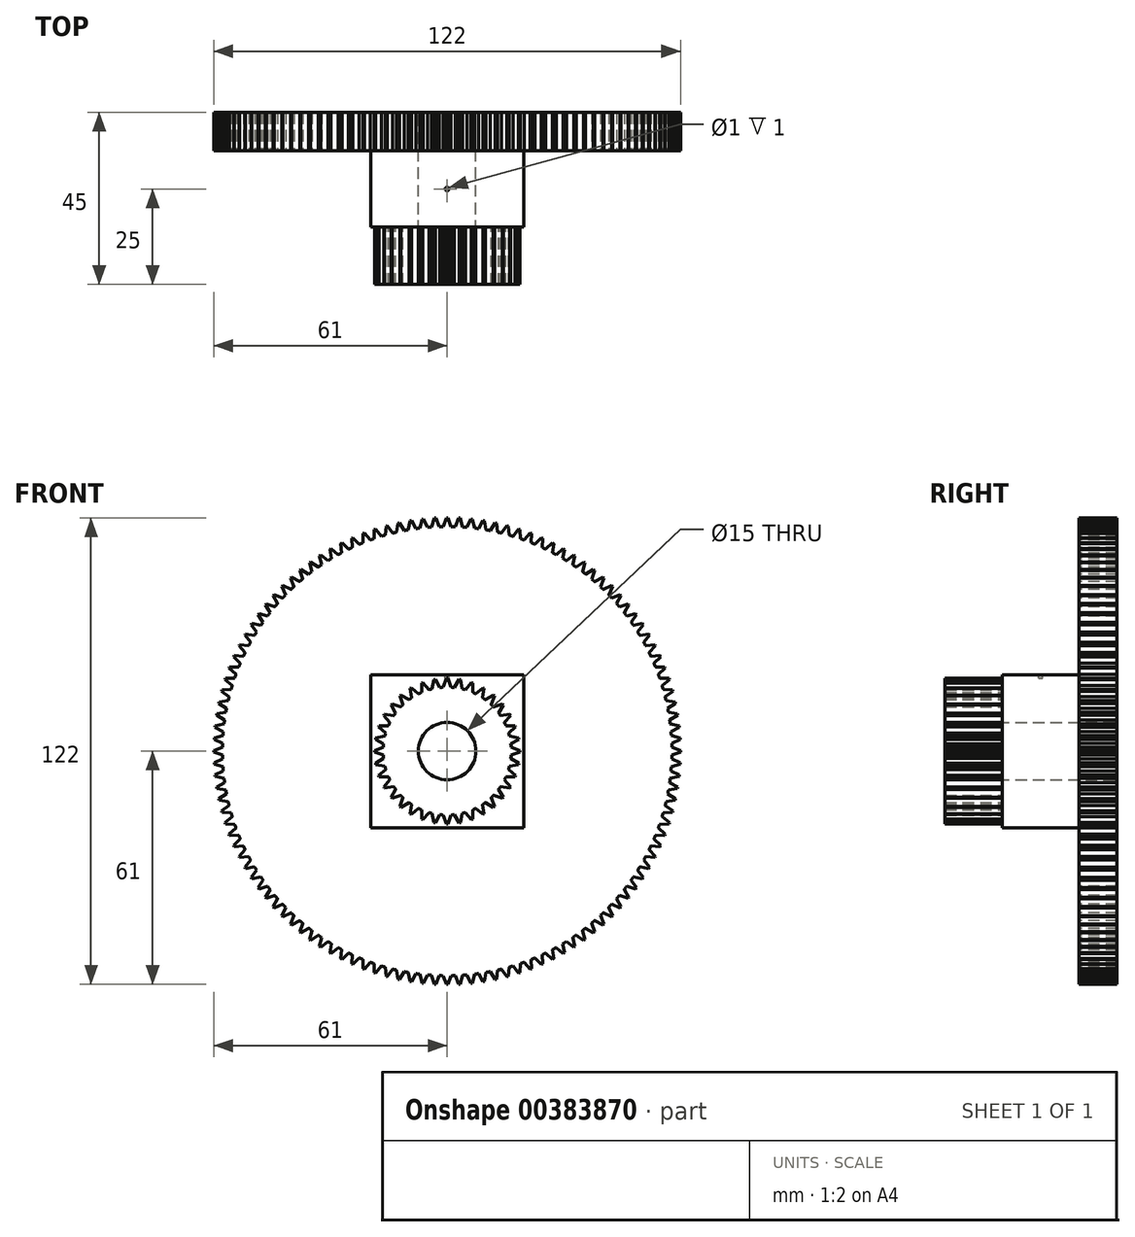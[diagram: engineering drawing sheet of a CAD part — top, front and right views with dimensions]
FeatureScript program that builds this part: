
annotation { "Feature Type Name" : "Feature", "Feature Type Description" : "" }
export const myFeature = defineFeature(function(context is Context, id is Id, definition is map)
    precondition{}
    {
        {
            var Q0;
            Q0=qCreatedBy(makeId("Front.planeOp"),FACE);
            var sketch = newSketch(context, id + "F0", { "sketchPlane" : qUnion([Q0])});
            skCircle(sketch, "E0", {"center": v(0, 0) * mm, "radius": 7.5 * mm});
            skCircle(sketch, "E1", {"center": v(0, 0) * mm, "radius": 16.75 * mm});
            skCircle(sketch, "E2", {"center": v(0, 0) * mm, "radius": 19 * mm, "construction": true});
            skLineSegment(sketch, "E3", {"start": v(-1.02, 16.72) * mm, "end": v(-0.19, 19) * mm});
            skLineSegment(sketch, "E4", {"start": v(-0.19, 19) * mm, "end": v(0, 19) * mm});
            skLineSegment(sketch, "E5", {"start": v(-1.02, 16.72) * mm, "end": v(-1.02, 19.93) * mm, "construction": true});
            skLineSegment(sketch, "E6.MirrorCS", {"start": v(0.19, 19) * mm, "end": v(0, 19) * mm});
            skLineSegment(sketch, "E7.MirrorCS", {"start": v(1.02, 16.72) * mm, "end": v(0.19, 19) * mm});
            skLineSegment(sketch, "E8.1.0", {"start": v(-3.9, 16.29) * mm, "end": v(-3.48, 18.68) * mm});
            skLineSegment(sketch, "E8.1.1", {"start": v(-3.48, 18.68) * mm, "end": v(-3.3, 18.71) * mm});
            skLineSegment(sketch, "E8.1.2", {"start": v(-3.11, 18.74) * mm, "end": v(-3.3, 18.71) * mm});
            skLineSegment(sketch, "E8.1.3", {"start": v(-1.9, 16.64) * mm, "end": v(-3.11, 18.74) * mm});
            skLineSegment(sketch, "E8.2.0", {"start": v(-6.67, 15.36) * mm, "end": v(-6.67, 17.8) * mm});
            skLineSegment(sketch, "E8.2.1", {"start": v(-6.67, 17.8) * mm, "end": v(-6.5, 17.85) * mm});
            skLineSegment(sketch, "E8.2.2", {"start": v(-6.32, 17.92) * mm, "end": v(-6.5, 17.85) * mm});
            skLineSegment(sketch, "E8.2.3", {"start": v(-4.76, 16.06) * mm, "end": v(-6.32, 17.92) * mm});
            skLineSegment(sketch, "E8.3.0", {"start": v(-9.24, 13.97) * mm, "end": v(-9.66, 16.36) * mm});
            skLineSegment(sketch, "E8.3.1", {"start": v(-9.66, 16.36) * mm, "end": v(-9.5, 16.45) * mm});
            skLineSegment(sketch, "E8.3.2", {"start": v(-9.34, 16.55) * mm, "end": v(-9.5, 16.45) * mm});
            skLineSegment(sketch, "E8.3.3", {"start": v(-7.48, 14.99) * mm, "end": v(-9.34, 16.55) * mm});
            skLineSegment(sketch, "E8.4.0", {"start": v(-11.53, 12.15) * mm, "end": v(-12.36, 14.43) * mm});
            skLineSegment(sketch, "E8.4.1", {"start": v(-12.36, 14.43) * mm, "end": v(-12.21, 14.55) * mm});
            skLineSegment(sketch, "E8.4.2", {"start": v(-12.07, 14.68) * mm, "end": v(-12.21, 14.55) * mm});
            skLineSegment(sketch, "E8.4.3", {"start": v(-9.97, 13.46) * mm, "end": v(-12.07, 14.68) * mm});
            skLineSegment(sketch, "E8.5.0", {"start": v(-13.46, 9.97) * mm, "end": v(-14.68, 12.07) * mm});
            skLineSegment(sketch, "E8.5.1", {"start": v(-14.68, 12.07) * mm, "end": v(-14.55, 12.21) * mm});
            skLineSegment(sketch, "E8.5.2", {"start": v(-14.43, 12.36) * mm, "end": v(-14.55, 12.21) * mm});
            skLineSegment(sketch, "E8.5.3", {"start": v(-12.15, 11.53) * mm, "end": v(-14.43, 12.36) * mm});
            skLineSegment(sketch, "E8.6.0", {"start": v(-14.99, 7.48) * mm, "end": v(-16.55, 9.34) * mm});
            skLineSegment(sketch, "E8.6.1", {"start": v(-16.55, 9.34) * mm, "end": v(-16.45, 9.5) * mm});
            skLineSegment(sketch, "E8.6.2", {"start": v(-16.36, 9.66) * mm, "end": v(-16.45, 9.5) * mm});
            skLineSegment(sketch, "E8.6.3", {"start": v(-13.97, 9.24) * mm, "end": v(-16.36, 9.66) * mm});
            skLineSegment(sketch, "E8.7.0", {"start": v(-16.06, 4.76) * mm, "end": v(-17.92, 6.32) * mm});
            skLineSegment(sketch, "E8.7.1", {"start": v(-17.92, 6.32) * mm, "end": v(-17.85, 6.5) * mm});
            skLineSegment(sketch, "E8.7.2", {"start": v(-17.8, 6.67) * mm, "end": v(-17.85, 6.5) * mm});
            skLineSegment(sketch, "E8.7.3", {"start": v(-15.36, 6.67) * mm, "end": v(-17.8, 6.67) * mm});
            skLineSegment(sketch, "E8.8.0", {"start": v(-16.64, 1.9) * mm, "end": v(-18.74, 3.11) * mm});
            skLineSegment(sketch, "E8.8.1", {"start": v(-18.74, 3.11) * mm, "end": v(-18.71, 3.3) * mm});
            skLineSegment(sketch, "E8.8.2", {"start": v(-18.68, 3.48) * mm, "end": v(-18.71, 3.3) * mm});
            skLineSegment(sketch, "E8.8.3", {"start": v(-16.29, 3.9) * mm, "end": v(-18.68, 3.48) * mm});
            skLineSegment(sketch, "E8.9.0", {"start": v(-16.72, -1.02) * mm, "end": v(-19, -0.19) * mm});
            skLineSegment(sketch, "E8.9.1", {"start": v(-19, -0.19) * mm, "end": v(-19, 0) * mm});
            skLineSegment(sketch, "E8.9.2", {"start": v(-19, 0.19) * mm, "end": v(-19, 0) * mm});
            skLineSegment(sketch, "E8.9.3", {"start": v(-16.72, 1.02) * mm, "end": v(-19, 0.19) * mm});
            skLineSegment(sketch, "E8.10.0", {"start": v(-16.29, -3.9) * mm, "end": v(-18.68, -3.48) * mm});
            skLineSegment(sketch, "E8.10.1", {"start": v(-18.68, -3.48) * mm, "end": v(-18.71, -3.3) * mm});
            skLineSegment(sketch, "E8.10.2", {"start": v(-18.74, -3.11) * mm, "end": v(-18.71, -3.3) * mm});
            skLineSegment(sketch, "E8.10.3", {"start": v(-16.64, -1.9) * mm, "end": v(-18.74, -3.11) * mm});
            skLineSegment(sketch, "E8.11.0", {"start": v(-15.36, -6.67) * mm, "end": v(-17.8, -6.67) * mm});
            skLineSegment(sketch, "E8.11.1", {"start": v(-17.8, -6.67) * mm, "end": v(-17.85, -6.5) * mm});
            skLineSegment(sketch, "E8.11.2", {"start": v(-17.92, -6.32) * mm, "end": v(-17.85, -6.5) * mm});
            skLineSegment(sketch, "E8.11.3", {"start": v(-16.06, -4.76) * mm, "end": v(-17.92, -6.32) * mm});
            skLineSegment(sketch, "E9.1.12.0", {"start": v(-13.97, -9.24) * mm, "end": v(-16.36, -9.66) * mm});
            skLineSegment(sketch, "E9.3.12.0", {"start": v(-16.36, -9.66) * mm, "end": v(-16.45, -9.5) * mm});
            skLineSegment(sketch, "E9.6.12.0", {"start": v(-16.55, -9.34) * mm, "end": v(-16.45, -9.5) * mm});
            skLineSegment(sketch, "E9.9.12.0", {"start": v(-14.99, -7.48) * mm, "end": v(-16.55, -9.34) * mm});
            skLineSegment(sketch, "E9.1.13.0", {"start": v(-12.15, -11.53) * mm, "end": v(-14.43, -12.36) * mm});
            skLineSegment(sketch, "E9.3.13.0", {"start": v(-14.43, -12.36) * mm, "end": v(-14.55, -12.21) * mm});
            skLineSegment(sketch, "E9.6.13.0", {"start": v(-14.68, -12.07) * mm, "end": v(-14.55, -12.21) * mm});
            skLineSegment(sketch, "E9.9.13.0", {"start": v(-13.46, -9.97) * mm, "end": v(-14.68, -12.07) * mm});
            skLineSegment(sketch, "E9.1.14.0", {"start": v(-9.97, -13.46) * mm, "end": v(-12.07, -14.68) * mm});
            skLineSegment(sketch, "E9.3.14.0", {"start": v(-12.07, -14.68) * mm, "end": v(-12.21, -14.55) * mm});
            skLineSegment(sketch, "E9.6.14.0", {"start": v(-12.36, -14.43) * mm, "end": v(-12.21, -14.55) * mm});
            skLineSegment(sketch, "E9.9.14.0", {"start": v(-11.53, -12.15) * mm, "end": v(-12.36, -14.43) * mm});
            skLineSegment(sketch, "E9.1.15.0", {"start": v(-7.48, -14.99) * mm, "end": v(-9.34, -16.55) * mm});
            skLineSegment(sketch, "E9.3.15.0", {"start": v(-9.34, -16.55) * mm, "end": v(-9.5, -16.45) * mm});
            skLineSegment(sketch, "E9.6.15.0", {"start": v(-9.66, -16.36) * mm, "end": v(-9.5, -16.45) * mm});
            skLineSegment(sketch, "E9.9.15.0", {"start": v(-9.24, -13.97) * mm, "end": v(-9.66, -16.36) * mm});
            skLineSegment(sketch, "E9.1.16.0", {"start": v(-4.76, -16.06) * mm, "end": v(-6.32, -17.92) * mm});
            skLineSegment(sketch, "E9.3.16.0", {"start": v(-6.32, -17.92) * mm, "end": v(-6.5, -17.85) * mm});
            skLineSegment(sketch, "E9.6.16.0", {"start": v(-6.67, -17.8) * mm, "end": v(-6.5, -17.85) * mm});
            skLineSegment(sketch, "E9.9.16.0", {"start": v(-6.67, -15.36) * mm, "end": v(-6.67, -17.8) * mm});
            skLineSegment(sketch, "E9.1.17.0", {"start": v(-1.9, -16.64) * mm, "end": v(-3.11, -18.74) * mm});
            skLineSegment(sketch, "E9.3.17.0", {"start": v(-3.11, -18.74) * mm, "end": v(-3.3, -18.71) * mm});
            skLineSegment(sketch, "E9.6.17.0", {"start": v(-3.48, -18.68) * mm, "end": v(-3.3, -18.71) * mm});
            skLineSegment(sketch, "E9.9.17.0", {"start": v(-3.9, -16.29) * mm, "end": v(-3.48, -18.68) * mm});
            skLineSegment(sketch, "E9.1.18.0", {"start": v(1.02, -16.72) * mm, "end": v(0.19, -19) * mm});
            skLineSegment(sketch, "E9.3.18.0", {"start": v(0.19, -19) * mm, "end": v(0, -19) * mm});
            skLineSegment(sketch, "E9.6.18.0", {"start": v(-0.19, -19) * mm, "end": v(0, -19) * mm});
            skLineSegment(sketch, "E9.9.18.0", {"start": v(-1.02, -16.72) * mm, "end": v(-0.19, -19) * mm});
            skLineSegment(sketch, "E9.1.19.0", {"start": v(3.9, -16.29) * mm, "end": v(3.48, -18.68) * mm});
            skLineSegment(sketch, "E9.3.19.0", {"start": v(3.48, -18.68) * mm, "end": v(3.3, -18.71) * mm});
            skLineSegment(sketch, "E9.6.19.0", {"start": v(3.11, -18.74) * mm, "end": v(3.3, -18.71) * mm});
            skLineSegment(sketch, "E9.9.19.0", {"start": v(1.9, -16.64) * mm, "end": v(3.11, -18.74) * mm});
            skLineSegment(sketch, "E9.1.20.0", {"start": v(6.67, -15.36) * mm, "end": v(6.67, -17.8) * mm});
            skLineSegment(sketch, "E9.3.20.0", {"start": v(6.67, -17.8) * mm, "end": v(6.5, -17.85) * mm});
            skLineSegment(sketch, "E9.6.20.0", {"start": v(6.32, -17.92) * mm, "end": v(6.5, -17.85) * mm});
            skLineSegment(sketch, "E9.9.20.0", {"start": v(4.76, -16.06) * mm, "end": v(6.32, -17.92) * mm});
            skLineSegment(sketch, "E9.1.21.0", {"start": v(9.24, -13.97) * mm, "end": v(9.66, -16.36) * mm});
            skLineSegment(sketch, "E9.3.21.0", {"start": v(9.66, -16.36) * mm, "end": v(9.5, -16.45) * mm});
            skLineSegment(sketch, "E9.6.21.0", {"start": v(9.34, -16.55) * mm, "end": v(9.5, -16.45) * mm});
            skLineSegment(sketch, "E9.9.21.0", {"start": v(7.48, -14.99) * mm, "end": v(9.34, -16.55) * mm});
            skLineSegment(sketch, "E9.1.22.0", {"start": v(11.53, -12.15) * mm, "end": v(12.36, -14.43) * mm});
            skLineSegment(sketch, "E9.3.22.0", {"start": v(12.36, -14.43) * mm, "end": v(12.21, -14.55) * mm});
            skLineSegment(sketch, "E9.6.22.0", {"start": v(12.07, -14.68) * mm, "end": v(12.21, -14.55) * mm});
            skLineSegment(sketch, "E9.9.22.0", {"start": v(9.97, -13.46) * mm, "end": v(12.07, -14.68) * mm});
            skLineSegment(sketch, "E9.1.23.0", {"start": v(13.46, -9.97) * mm, "end": v(14.68, -12.07) * mm});
            skLineSegment(sketch, "E9.3.23.0", {"start": v(14.68, -12.07) * mm, "end": v(14.55, -12.21) * mm});
            skLineSegment(sketch, "E9.6.23.0", {"start": v(14.43, -12.36) * mm, "end": v(14.55, -12.21) * mm});
            skLineSegment(sketch, "E9.9.23.0", {"start": v(12.15, -11.53) * mm, "end": v(14.43, -12.36) * mm});
            skLineSegment(sketch, "E10.1.24.0", {"start": v(14.99, -7.48) * mm, "end": v(16.55, -9.34) * mm});
            skLineSegment(sketch, "E10.3.24.0", {"start": v(16.55, -9.34) * mm, "end": v(16.45, -9.5) * mm});
            skLineSegment(sketch, "E10.6.24.0", {"start": v(16.36, -9.66) * mm, "end": v(16.45, -9.5) * mm});
            skLineSegment(sketch, "E10.9.24.0", {"start": v(13.97, -9.24) * mm, "end": v(16.36, -9.66) * mm});
            skLineSegment(sketch, "E10.1.25.0", {"start": v(16.06, -4.76) * mm, "end": v(17.92, -6.32) * mm});
            skLineSegment(sketch, "E10.3.25.0", {"start": v(17.92, -6.32) * mm, "end": v(17.85, -6.5) * mm});
            skLineSegment(sketch, "E10.6.25.0", {"start": v(17.8, -6.67) * mm, "end": v(17.85, -6.5) * mm});
            skLineSegment(sketch, "E10.9.25.0", {"start": v(15.36, -6.67) * mm, "end": v(17.8, -6.67) * mm});
            skLineSegment(sketch, "E10.1.26.0", {"start": v(16.64, -1.9) * mm, "end": v(18.74, -3.11) * mm});
            skLineSegment(sketch, "E10.3.26.0", {"start": v(18.74, -3.11) * mm, "end": v(18.71, -3.3) * mm});
            skLineSegment(sketch, "E10.6.26.0", {"start": v(18.68, -3.48) * mm, "end": v(18.71, -3.3) * mm});
            skLineSegment(sketch, "E10.9.26.0", {"start": v(16.29, -3.9) * mm, "end": v(18.68, -3.48) * mm});
            skLineSegment(sketch, "E10.1.27.0", {"start": v(16.72, 1.02) * mm, "end": v(19, 0.19) * mm});
            skLineSegment(sketch, "E10.3.27.0", {"start": v(19, 0.19) * mm, "end": v(19, 0) * mm});
            skLineSegment(sketch, "E10.6.27.0", {"start": v(19, -0.19) * mm, "end": v(19, 0) * mm});
            skLineSegment(sketch, "E10.9.27.0", {"start": v(16.72, -1.02) * mm, "end": v(19, -0.19) * mm});
            skLineSegment(sketch, "E10.1.28.0", {"start": v(16.29, 3.9) * mm, "end": v(18.68, 3.48) * mm});
            skLineSegment(sketch, "E10.3.28.0", {"start": v(18.68, 3.48) * mm, "end": v(18.71, 3.3) * mm});
            skLineSegment(sketch, "E10.6.28.0", {"start": v(18.74, 3.11) * mm, "end": v(18.71, 3.3) * mm});
            skLineSegment(sketch, "E10.9.28.0", {"start": v(16.64, 1.9) * mm, "end": v(18.74, 3.11) * mm});
            skLineSegment(sketch, "E10.1.29.0", {"start": v(15.36, 6.67) * mm, "end": v(17.8, 6.67) * mm});
            skLineSegment(sketch, "E10.3.29.0", {"start": v(17.8, 6.67) * mm, "end": v(17.85, 6.5) * mm});
            skLineSegment(sketch, "E10.6.29.0", {"start": v(17.92, 6.32) * mm, "end": v(17.85, 6.5) * mm});
            skLineSegment(sketch, "E10.9.29.0", {"start": v(16.06, 4.76) * mm, "end": v(17.92, 6.32) * mm});
            skLineSegment(sketch, "E10.1.30.0", {"start": v(13.97, 9.24) * mm, "end": v(16.36, 9.66) * mm});
            skLineSegment(sketch, "E10.3.30.0", {"start": v(16.36, 9.66) * mm, "end": v(16.45, 9.5) * mm});
            skLineSegment(sketch, "E10.6.30.0", {"start": v(16.55, 9.34) * mm, "end": v(16.45, 9.5) * mm});
            skLineSegment(sketch, "E10.9.30.0", {"start": v(14.99, 7.48) * mm, "end": v(16.55, 9.34) * mm});
            skLineSegment(sketch, "E10.1.31.0", {"start": v(12.15, 11.53) * mm, "end": v(14.43, 12.36) * mm});
            skLineSegment(sketch, "E10.3.31.0", {"start": v(14.43, 12.36) * mm, "end": v(14.55, 12.21) * mm});
            skLineSegment(sketch, "E10.6.31.0", {"start": v(14.68, 12.07) * mm, "end": v(14.55, 12.21) * mm});
            skLineSegment(sketch, "E10.9.31.0", {"start": v(13.46, 9.97) * mm, "end": v(14.68, 12.07) * mm});
            skLineSegment(sketch, "E10.1.32.0", {"start": v(9.97, 13.46) * mm, "end": v(12.07, 14.68) * mm});
            skLineSegment(sketch, "E10.3.32.0", {"start": v(12.07, 14.68) * mm, "end": v(12.21, 14.55) * mm});
            skLineSegment(sketch, "E10.6.32.0", {"start": v(12.36, 14.43) * mm, "end": v(12.21, 14.55) * mm});
            skLineSegment(sketch, "E10.9.32.0", {"start": v(11.53, 12.15) * mm, "end": v(12.36, 14.43) * mm});
            skLineSegment(sketch, "E10.1.33.0", {"start": v(7.48, 14.99) * mm, "end": v(9.34, 16.55) * mm});
            skLineSegment(sketch, "E10.3.33.0", {"start": v(9.34, 16.55) * mm, "end": v(9.5, 16.45) * mm});
            skLineSegment(sketch, "E10.6.33.0", {"start": v(9.66, 16.36) * mm, "end": v(9.5, 16.45) * mm});
            skLineSegment(sketch, "E10.9.33.0", {"start": v(9.24, 13.97) * mm, "end": v(9.66, 16.36) * mm});
            skLineSegment(sketch, "E10.1.34.0", {"start": v(4.76, 16.06) * mm, "end": v(6.32, 17.92) * mm});
            skLineSegment(sketch, "E10.3.34.0", {"start": v(6.32, 17.92) * mm, "end": v(6.5, 17.85) * mm});
            skLineSegment(sketch, "E10.6.34.0", {"start": v(6.67, 17.8) * mm, "end": v(6.5, 17.85) * mm});
            skLineSegment(sketch, "E10.9.34.0", {"start": v(6.67, 15.36) * mm, "end": v(6.67, 17.8) * mm});
            skLineSegment(sketch, "E10.1.35.0", {"start": v(1.9, 16.64) * mm, "end": v(3.11, 18.74) * mm});
            skLineSegment(sketch, "E10.3.35.0", {"start": v(3.11, 18.74) * mm, "end": v(3.3, 18.71) * mm});
            skLineSegment(sketch, "E10.6.35.0", {"start": v(3.48, 18.68) * mm, "end": v(3.3, 18.71) * mm});
            skLineSegment(sketch, "E10.9.35.0", {"start": v(3.9, 16.29) * mm, "end": v(3.48, 18.68) * mm});
            skSolve(sketch);
        }
        {
            var Q0;
            Q0=qSketchRegion(id+"F0",true);
            extrude(context, id + "F1", {"entities" : qUnion([Q0]), "depth" : 15 * mm});
        }
        {
            var Q0;
            Q0=qCreatedBy(makeId("Front.planeOp"),FACE);
            var sketch = newSketch(context, id + "F2", { "sketchPlane" : qUnion([Q0])});
            skCircle(sketch, "E11", {"center": v(0, 0) * mm, "radius": 7.5 * mm});
            skLineSegment(sketch, "E12.bottom", {"start": v(-20, -20) * mm, "end": v(20, -20) * mm});
            skLineSegment(sketch, "E12.top", {"start": v(-20, 20) * mm, "end": v(20, 20) * mm});
            skLineSegment(sketch, "E12.left", {"start": v(-20, -20) * mm, "end": v(-20, 20) * mm});
            skLineSegment(sketch, "E12.right", {"start": v(20, -20) * mm, "end": v(20, 20) * mm});
            skSolve(sketch);
        }
        {
            var Q0;
            Q0=qSketchRegion(id+"F2",true);
            extrude(context, id + "F3", {"entities" : qUnion([Q0]), "operationType" : NewBodyOperationType.ADD, "depth" : -20 * mm});
        }
        {
            var Q0;
            Q0=makeQuery(id+"F3.opExtrude","CAP_FACE",FACE,{"disambiguationData":[OSD([sQuery(id+"F2.wireOp",EDGE,"Zh5lLQ9h-1iR5-KiPg-C2Wr-JR3NM9Zv75rL"),sQuery(id+"F2.wireOp",EDGE,"E11")])],"isStart":false});
            var sketch = newSketch(context, id + "F4", { "sketchPlane" : qUnion([Q0])});
            skCircle(sketch, "E13", {"center": v(0, 0) * mm, "radius": 58.75 * mm});
            skCircle(sketch, "E14", {"center": v(0, 0) * mm, "radius": 61 * mm, "construction": true});
            skLineSegment(sketch, "E15", {"start": v(-1, 58.74) * mm, "end": v(-1, 64.16) * mm, "construction": true});
            skLineSegment(sketch, "E16", {"start": v(-1, 58.74) * mm, "end": v(-0.19, 61) * mm});
            skLineSegment(sketch, "E17", {"start": v(-0.19, 61) * mm, "end": v(0, 61) * mm});
            skLineSegment(sketch, "E18.MirrorCS", {"start": v(0.19, 61) * mm, "end": v(0, 61) * mm});
            skLineSegment(sketch, "E19.MirrorCS", {"start": v(1, 58.74) * mm, "end": v(0.19, 61) * mm});
            skLineSegment(sketch, "E20.1.0", {"start": v(-4.08, 58.6) * mm, "end": v(-3.38, 60.9) * mm});
            skLineSegment(sketch, "E20.1.1", {"start": v(-3.38, 60.9) * mm, "end": v(-3.2, 60.92) * mm});
            skLineSegment(sketch, "E20.1.2", {"start": v(-3, 60.93) * mm, "end": v(-3.2, 60.92) * mm});
            skLineSegment(sketch, "E20.1.3", {"start": v(-2.07, 58.71) * mm, "end": v(-3, 60.93) * mm});
            skLineSegment(sketch, "E20.2.0", {"start": v(-7.14, 58.31) * mm, "end": v(-6.56, 60.65) * mm});
            skLineSegment(sketch, "E20.2.1", {"start": v(-6.56, 60.65) * mm, "end": v(-6.38, 60.67) * mm});
            skLineSegment(sketch, "E20.2.2", {"start": v(-6.19, 60.69) * mm, "end": v(-6.38, 60.67) * mm});
            skLineSegment(sketch, "E20.2.3", {"start": v(-5.14, 58.53) * mm, "end": v(-6.19, 60.69) * mm});
            skLineSegment(sketch, "E20.3.0", {"start": v(-10.19, 57.86) * mm, "end": v(-9.73, 60.22) * mm});
            skLineSegment(sketch, "E20.3.1", {"start": v(-9.73, 60.22) * mm, "end": v(-9.54, 60.25) * mm});
            skLineSegment(sketch, "E20.3.2", {"start": v(-9.36, 60.28) * mm, "end": v(-9.54, 60.25) * mm});
            skLineSegment(sketch, "E20.3.3", {"start": v(-8.2, 58.18) * mm, "end": v(-9.36, 60.28) * mm});
            skLineSegment(sketch, "E20.4.0", {"start": v(-13.2, 57.25) * mm, "end": v(-12.87, 59.63) * mm});
            skLineSegment(sketch, "E20.4.1", {"start": v(-12.87, 59.63) * mm, "end": v(-12.68, 59.67) * mm});
            skLineSegment(sketch, "E20.4.2", {"start": v(-12.5, 59.7) * mm, "end": v(-12.68, 59.67) * mm});
            skLineSegment(sketch, "E20.4.3", {"start": v(-11.23, 57.67) * mm, "end": v(-12.5, 59.7) * mm});
            skLineSegment(sketch, "E20.5.0", {"start": v(-16.18, 56.48) * mm, "end": v(-15.97, 58.87) * mm});
            skLineSegment(sketch, "E20.5.1", {"start": v(-15.97, 58.87) * mm, "end": v(-15.79, 58.92) * mm});
            skLineSegment(sketch, "E20.5.2", {"start": v(-15.6, 58.97) * mm, "end": v(-15.79, 58.92) * mm});
            skLineSegment(sketch, "E20.5.3", {"start": v(-14.23, 57) * mm, "end": v(-15.6, 58.97) * mm});
            skLineSegment(sketch, "E20.6.0", {"start": v(-19.11, 55.55) * mm, "end": v(-19.03, 57.96) * mm});
            skLineSegment(sketch, "E20.6.1", {"start": v(-19.03, 57.96) * mm, "end": v(-18.85, 58.01) * mm});
            skLineSegment(sketch, "E20.6.2", {"start": v(-18.67, 58.07) * mm, "end": v(-18.85, 58.01) * mm});
            skLineSegment(sketch, "E20.6.3", {"start": v(-17.2, 56.18) * mm, "end": v(-18.67, 58.07) * mm});
            skLineSegment(sketch, "E20.7.0", {"start": v(-22, 54.48) * mm, "end": v(-22.04, 56.88) * mm});
            skLineSegment(sketch, "E20.7.1", {"start": v(-22.04, 56.88) * mm, "end": v(-21.86, 56.95) * mm});
            skLineSegment(sketch, "E20.7.2", {"start": v(-21.69, 57.02) * mm, "end": v(-21.86, 56.95) * mm});
            skLineSegment(sketch, "E20.7.3", {"start": v(-20.1, 55.2) * mm, "end": v(-21.69, 57.02) * mm});
            skLineSegment(sketch, "E20.8.0", {"start": v(-24.81, 53.25) * mm, "end": v(-24.98, 55.65) * mm});
            skLineSegment(sketch, "E20.8.1", {"start": v(-24.98, 55.65) * mm, "end": v(-24.81, 55.73) * mm});
            skLineSegment(sketch, "E20.8.2", {"start": v(-24.64, 55.8) * mm, "end": v(-24.81, 55.73) * mm});
            skLineSegment(sketch, "E20.8.3", {"start": v(-22.97, 54.07) * mm, "end": v(-24.64, 55.8) * mm});
            skLineSegment(sketch, "E20.9.0", {"start": v(-27.57, 51.88) * mm, "end": v(-27.86, 54.27) * mm});
            skLineSegment(sketch, "E20.9.1", {"start": v(-27.86, 54.27) * mm, "end": v(-27.7, 54.35) * mm});
            skLineSegment(sketch, "E20.9.2", {"start": v(-27.53, 54.44) * mm, "end": v(-27.7, 54.35) * mm});
            skLineSegment(sketch, "E20.9.3", {"start": v(-25.77, 52.8) * mm, "end": v(-27.53, 54.44) * mm});
            skLineSegment(sketch, "E20.10.0", {"start": v(-30.24, 50.37) * mm, "end": v(-30.66, 52.73) * mm});
            skLineSegment(sketch, "E20.10.1", {"start": v(-30.66, 52.73) * mm, "end": v(-30.5, 52.83) * mm});
            skLineSegment(sketch, "E20.10.2", {"start": v(-30.34, 52.92) * mm, "end": v(-30.5, 52.83) * mm});
            skLineSegment(sketch, "E20.10.3", {"start": v(-28.5, 51.38) * mm, "end": v(-30.34, 52.92) * mm});
            skLineSegment(sketch, "E20.11.0", {"start": v(-32.84, 48.71) * mm, "end": v(-33.38, 51.06) * mm});
            skLineSegment(sketch, "E20.11.1", {"start": v(-33.38, 51.06) * mm, "end": v(-33.22, 51.16) * mm});
            skLineSegment(sketch, "E20.11.2", {"start": v(-33.07, 51.26) * mm, "end": v(-33.22, 51.16) * mm});
            skLineSegment(sketch, "E20.11.3", {"start": v(-31.15, 49.81) * mm, "end": v(-33.07, 51.26) * mm});
            skLineSegment(sketch, "E20.12.0", {"start": v(-35.34, 46.93) * mm, "end": v(-36, 49.24) * mm});
            skLineSegment(sketch, "E20.12.1", {"start": v(-36, 49.24) * mm, "end": v(-35.85, 49.35) * mm});
            skLineSegment(sketch, "E20.12.2", {"start": v(-35.7, 49.46) * mm, "end": v(-35.85, 49.35) * mm});
            skLineSegment(sketch, "E20.12.3", {"start": v(-33.71, 48.12) * mm, "end": v(-35.7, 49.46) * mm});
            skLineSegment(sketch, "E20.13.0", {"start": v(-37.75, 45.02) * mm, "end": v(-38.53, 47.29) * mm});
            skLineSegment(sketch, "E20.13.1", {"start": v(-38.53, 47.29) * mm, "end": v(-38.39, 47.4) * mm});
            skLineSegment(sketch, "E20.13.2", {"start": v(-38.24, 47.52) * mm, "end": v(-38.39, 47.4) * mm});
            skLineSegment(sketch, "E20.13.3", {"start": v(-36.18, 46.29) * mm, "end": v(-38.24, 47.52) * mm});
            skLineSegment(sketch, "E20.14.0", {"start": v(-40.06, 42.98) * mm, "end": v(-40.96, 45.2) * mm});
            skLineSegment(sketch, "E20.14.1", {"start": v(-40.96, 45.2) * mm, "end": v(-40.82, 45.33) * mm});
            skLineSegment(sketch, "E20.14.2", {"start": v(-40.68, 45.46) * mm, "end": v(-40.82, 45.33) * mm});
            skLineSegment(sketch, "E20.14.3", {"start": v(-38.56, 44.33) * mm, "end": v(-40.68, 45.46) * mm});
            skLineSegment(sketch, "E20.15.0", {"start": v(-42.25, 40.82) * mm, "end": v(-43.27, 43) * mm});
            skLineSegment(sketch, "E20.15.1", {"start": v(-43.27, 43) * mm, "end": v(-43.13, 43.13) * mm});
            skLineSegment(sketch, "E20.15.2", {"start": v(-43, 43.27) * mm, "end": v(-43.13, 43.13) * mm});
            skLineSegment(sketch, "E20.15.3", {"start": v(-40.82, 42.25) * mm, "end": v(-43, 43.27) * mm});
            skLineSegment(sketch, "E20.16.0", {"start": v(-44.33, 38.56) * mm, "end": v(-45.46, 40.68) * mm});
            skLineSegment(sketch, "E20.16.1", {"start": v(-45.46, 40.68) * mm, "end": v(-45.33, 40.82) * mm});
            skLineSegment(sketch, "E20.16.2", {"start": v(-45.2, 40.96) * mm, "end": v(-45.33, 40.82) * mm});
            skLineSegment(sketch, "E20.16.3", {"start": v(-42.98, 40.06) * mm, "end": v(-45.2, 40.96) * mm});
            skLineSegment(sketch, "E20.17.0", {"start": v(-46.29, 36.18) * mm, "end": v(-47.52, 38.24) * mm});
            skLineSegment(sketch, "E20.17.1", {"start": v(-47.52, 38.24) * mm, "end": v(-47.4, 38.39) * mm});
            skLineSegment(sketch, "E20.17.2", {"start": v(-47.29, 38.53) * mm, "end": v(-47.4, 38.39) * mm});
            skLineSegment(sketch, "E20.17.3", {"start": v(-45.02, 37.75) * mm, "end": v(-47.29, 38.53) * mm});
            skLineSegment(sketch, "E20.18.0", {"start": v(-48.12, 33.71) * mm, "end": v(-49.46, 35.7) * mm});
            skLineSegment(sketch, "E20.18.1", {"start": v(-49.46, 35.7) * mm, "end": v(-49.35, 35.85) * mm});
            skLineSegment(sketch, "E20.18.2", {"start": v(-49.24, 36) * mm, "end": v(-49.35, 35.85) * mm});
            skLineSegment(sketch, "E20.18.3", {"start": v(-46.93, 35.34) * mm, "end": v(-49.24, 36) * mm});
            skLineSegment(sketch, "E20.19.0", {"start": v(-49.81, 31.15) * mm, "end": v(-51.26, 33.07) * mm});
            skLineSegment(sketch, "E20.19.1", {"start": v(-51.26, 33.07) * mm, "end": v(-51.16, 33.22) * mm});
            skLineSegment(sketch, "E20.19.2", {"start": v(-51.06, 33.38) * mm, "end": v(-51.16, 33.22) * mm});
            skLineSegment(sketch, "E20.19.3", {"start": v(-48.71, 32.84) * mm, "end": v(-51.06, 33.38) * mm});
            skLineSegment(sketch, "E20.20.0", {"start": v(-51.38, 28.5) * mm, "end": v(-52.92, 30.34) * mm});
            skLineSegment(sketch, "E20.20.1", {"start": v(-52.92, 30.34) * mm, "end": v(-52.83, 30.5) * mm});
            skLineSegment(sketch, "E20.20.2", {"start": v(-52.73, 30.66) * mm, "end": v(-52.83, 30.5) * mm});
            skLineSegment(sketch, "E20.20.3", {"start": v(-50.37, 30.24) * mm, "end": v(-52.73, 30.66) * mm});
            skLineSegment(sketch, "E20.21.0", {"start": v(-52.8, 25.77) * mm, "end": v(-54.44, 27.53) * mm});
            skLineSegment(sketch, "E20.21.1", {"start": v(-54.44, 27.53) * mm, "end": v(-54.35, 27.7) * mm});
            skLineSegment(sketch, "E20.21.2", {"start": v(-54.27, 27.86) * mm, "end": v(-54.35, 27.7) * mm});
            skLineSegment(sketch, "E20.21.3", {"start": v(-51.88, 27.57) * mm, "end": v(-54.27, 27.86) * mm});
            skLineSegment(sketch, "E20.22.0", {"start": v(-54.07, 22.97) * mm, "end": v(-55.8, 24.64) * mm});
            skLineSegment(sketch, "E20.22.1", {"start": v(-55.8, 24.64) * mm, "end": v(-55.73, 24.81) * mm});
            skLineSegment(sketch, "E20.22.2", {"start": v(-55.65, 24.98) * mm, "end": v(-55.73, 24.81) * mm});
            skLineSegment(sketch, "E20.22.3", {"start": v(-53.25, 24.81) * mm, "end": v(-55.65, 24.98) * mm});
            skLineSegment(sketch, "E20.23.0", {"start": v(-55.2, 20.1) * mm, "end": v(-57.02, 21.69) * mm});
            skLineSegment(sketch, "E20.23.1", {"start": v(-57.02, 21.69) * mm, "end": v(-56.95, 21.86) * mm});
            skLineSegment(sketch, "E20.23.2", {"start": v(-56.88, 22.04) * mm, "end": v(-56.95, 21.86) * mm});
            skLineSegment(sketch, "E20.23.3", {"start": v(-54.48, 22) * mm, "end": v(-56.88, 22.04) * mm});
            skLineSegment(sketch, "E20.24.0", {"start": v(-56.18, 17.2) * mm, "end": v(-58.07, 18.67) * mm});
            skLineSegment(sketch, "E20.24.1", {"start": v(-58.07, 18.67) * mm, "end": v(-58.01, 18.85) * mm});
            skLineSegment(sketch, "E20.24.2", {"start": v(-57.96, 19.03) * mm, "end": v(-58.01, 18.85) * mm});
            skLineSegment(sketch, "E20.24.3", {"start": v(-55.55, 19.11) * mm, "end": v(-57.96, 19.03) * mm});
            skLineSegment(sketch, "E20.25.0", {"start": v(-57, 14.23) * mm, "end": v(-58.97, 15.6) * mm});
            skLineSegment(sketch, "E20.25.1", {"start": v(-58.97, 15.6) * mm, "end": v(-58.92, 15.79) * mm});
            skLineSegment(sketch, "E20.25.2", {"start": v(-58.87, 15.97) * mm, "end": v(-58.92, 15.79) * mm});
            skLineSegment(sketch, "E20.25.3", {"start": v(-56.48, 16.18) * mm, "end": v(-58.87, 15.97) * mm});
            skLineSegment(sketch, "E20.26.0", {"start": v(-57.67, 11.23) * mm, "end": v(-59.7, 12.5) * mm});
            skLineSegment(sketch, "E20.26.1", {"start": v(-59.7, 12.5) * mm, "end": v(-59.67, 12.68) * mm});
            skLineSegment(sketch, "E20.26.2", {"start": v(-59.63, 12.87) * mm, "end": v(-59.67, 12.68) * mm});
            skLineSegment(sketch, "E20.26.3", {"start": v(-57.25, 13.2) * mm, "end": v(-59.63, 12.87) * mm});
            skLineSegment(sketch, "E20.27.0", {"start": v(-58.18, 8.2) * mm, "end": v(-60.28, 9.36) * mm});
            skLineSegment(sketch, "E20.27.1", {"start": v(-60.28, 9.36) * mm, "end": v(-60.25, 9.54) * mm});
            skLineSegment(sketch, "E20.27.2", {"start": v(-60.22, 9.73) * mm, "end": v(-60.25, 9.54) * mm});
            skLineSegment(sketch, "E20.27.3", {"start": v(-57.86, 10.19) * mm, "end": v(-60.22, 9.73) * mm});
            skLineSegment(sketch, "E20.28.0", {"start": v(-58.53, 5.14) * mm, "end": v(-60.69, 6.19) * mm});
            skLineSegment(sketch, "E20.28.1", {"start": v(-60.69, 6.19) * mm, "end": v(-60.67, 6.38) * mm});
            skLineSegment(sketch, "E20.28.2", {"start": v(-60.65, 6.56) * mm, "end": v(-60.67, 6.38) * mm});
            skLineSegment(sketch, "E20.28.3", {"start": v(-58.31, 7.14) * mm, "end": v(-60.65, 6.56) * mm});
            skLineSegment(sketch, "E20.29.0", {"start": v(-58.71, 2.07) * mm, "end": v(-60.93, 3) * mm});
            skLineSegment(sketch, "E20.29.1", {"start": v(-60.93, 3) * mm, "end": v(-60.92, 3.2) * mm});
            skLineSegment(sketch, "E20.29.2", {"start": v(-60.9, 3.38) * mm, "end": v(-60.92, 3.2) * mm});
            skLineSegment(sketch, "E20.29.3", {"start": v(-58.6, 4.08) * mm, "end": v(-60.9, 3.38) * mm});
            skLineSegment(sketch, "E20.30.0", {"start": v(-58.74, -1) * mm, "end": v(-61, -0.19) * mm});
            skLineSegment(sketch, "E20.30.1", {"start": v(-61, -0.19) * mm, "end": v(-61, 0) * mm});
            skLineSegment(sketch, "E20.30.2", {"start": v(-61, 0.19) * mm, "end": v(-61, 0) * mm});
            skLineSegment(sketch, "E20.30.3", {"start": v(-58.74, 1) * mm, "end": v(-61, 0.19) * mm});
            skLineSegment(sketch, "E20.31.0", {"start": v(-58.6, -4.08) * mm, "end": v(-60.9, -3.38) * mm});
            skLineSegment(sketch, "E20.31.1", {"start": v(-60.9, -3.38) * mm, "end": v(-60.92, -3.2) * mm});
            skLineSegment(sketch, "E20.31.2", {"start": v(-60.93, -3) * mm, "end": v(-60.92, -3.2) * mm});
            skLineSegment(sketch, "E20.31.3", {"start": v(-58.71, -2.07) * mm, "end": v(-60.93, -3) * mm});
            skLineSegment(sketch, "E20.32.0", {"start": v(-58.31, -7.14) * mm, "end": v(-60.65, -6.56) * mm});
            skLineSegment(sketch, "E20.32.1", {"start": v(-60.65, -6.56) * mm, "end": v(-60.67, -6.38) * mm});
            skLineSegment(sketch, "E20.32.2", {"start": v(-60.69, -6.19) * mm, "end": v(-60.67, -6.38) * mm});
            skLineSegment(sketch, "E20.32.3", {"start": v(-58.53, -5.14) * mm, "end": v(-60.69, -6.19) * mm});
            skLineSegment(sketch, "E20.33.0", {"start": v(-57.86, -10.19) * mm, "end": v(-60.22, -9.73) * mm});
            skLineSegment(sketch, "E20.33.1", {"start": v(-60.22, -9.73) * mm, "end": v(-60.25, -9.54) * mm});
            skLineSegment(sketch, "E20.33.2", {"start": v(-60.28, -9.36) * mm, "end": v(-60.25, -9.54) * mm});
            skLineSegment(sketch, "E20.33.3", {"start": v(-58.18, -8.2) * mm, "end": v(-60.28, -9.36) * mm});
            skLineSegment(sketch, "E20.34.0", {"start": v(-57.25, -13.2) * mm, "end": v(-59.63, -12.87) * mm});
            skLineSegment(sketch, "E20.34.1", {"start": v(-59.63, -12.87) * mm, "end": v(-59.67, -12.68) * mm});
            skLineSegment(sketch, "E20.34.2", {"start": v(-59.7, -12.5) * mm, "end": v(-59.67, -12.68) * mm});
            skLineSegment(sketch, "E20.34.3", {"start": v(-57.67, -11.23) * mm, "end": v(-59.7, -12.5) * mm});
            skLineSegment(sketch, "E20.35.0", {"start": v(-56.48, -16.18) * mm, "end": v(-58.87, -15.97) * mm});
            skLineSegment(sketch, "E20.35.1", {"start": v(-58.87, -15.97) * mm, "end": v(-58.92, -15.79) * mm});
            skLineSegment(sketch, "E20.35.2", {"start": v(-58.97, -15.6) * mm, "end": v(-58.92, -15.79) * mm});
            skLineSegment(sketch, "E20.35.3", {"start": v(-57, -14.23) * mm, "end": v(-58.97, -15.6) * mm});
            skLineSegment(sketch, "E20.36.0", {"start": v(-55.55, -19.11) * mm, "end": v(-57.96, -19.03) * mm});
            skLineSegment(sketch, "E20.36.1", {"start": v(-57.96, -19.03) * mm, "end": v(-58.01, -18.85) * mm});
            skLineSegment(sketch, "E20.36.2", {"start": v(-58.07, -18.67) * mm, "end": v(-58.01, -18.85) * mm});
            skLineSegment(sketch, "E20.36.3", {"start": v(-56.18, -17.2) * mm, "end": v(-58.07, -18.67) * mm});
            skLineSegment(sketch, "E20.37.0", {"start": v(-54.48, -22) * mm, "end": v(-56.88, -22.04) * mm});
            skLineSegment(sketch, "E20.37.1", {"start": v(-56.88, -22.04) * mm, "end": v(-56.95, -21.86) * mm});
            skLineSegment(sketch, "E20.37.2", {"start": v(-57.02, -21.69) * mm, "end": v(-56.95, -21.86) * mm});
            skLineSegment(sketch, "E20.37.3", {"start": v(-55.2, -20.1) * mm, "end": v(-57.02, -21.69) * mm});
            skLineSegment(sketch, "E20.38.0", {"start": v(-53.25, -24.81) * mm, "end": v(-55.65, -24.98) * mm});
            skLineSegment(sketch, "E20.38.1", {"start": v(-55.65, -24.98) * mm, "end": v(-55.73, -24.81) * mm});
            skLineSegment(sketch, "E20.38.2", {"start": v(-55.8, -24.64) * mm, "end": v(-55.73, -24.81) * mm});
            skLineSegment(sketch, "E20.38.3", {"start": v(-54.07, -22.97) * mm, "end": v(-55.8, -24.64) * mm});
            skLineSegment(sketch, "E20.39.0", {"start": v(-51.88, -27.57) * mm, "end": v(-54.27, -27.86) * mm});
            skLineSegment(sketch, "E20.39.1", {"start": v(-54.27, -27.86) * mm, "end": v(-54.35, -27.7) * mm});
            skLineSegment(sketch, "E20.39.2", {"start": v(-54.44, -27.53) * mm, "end": v(-54.35, -27.7) * mm});
            skLineSegment(sketch, "E20.39.3", {"start": v(-52.8, -25.77) * mm, "end": v(-54.44, -27.53) * mm});
            skLineSegment(sketch, "E20.40.0", {"start": v(-50.37, -30.24) * mm, "end": v(-52.73, -30.66) * mm});
            skLineSegment(sketch, "E20.40.1", {"start": v(-52.73, -30.66) * mm, "end": v(-52.83, -30.5) * mm});
            skLineSegment(sketch, "E20.40.2", {"start": v(-52.92, -30.34) * mm, "end": v(-52.83, -30.5) * mm});
            skLineSegment(sketch, "E20.40.3", {"start": v(-51.38, -28.5) * mm, "end": v(-52.92, -30.34) * mm});
            skLineSegment(sketch, "E20.41.0", {"start": v(-48.71, -32.84) * mm, "end": v(-51.06, -33.38) * mm});
            skLineSegment(sketch, "E20.41.1", {"start": v(-51.06, -33.38) * mm, "end": v(-51.16, -33.22) * mm});
            skLineSegment(sketch, "E20.41.2", {"start": v(-51.26, -33.07) * mm, "end": v(-51.16, -33.22) * mm});
            skLineSegment(sketch, "E20.41.3", {"start": v(-49.81, -31.15) * mm, "end": v(-51.26, -33.07) * mm});
            skLineSegment(sketch, "E20.42.0", {"start": v(-46.93, -35.34) * mm, "end": v(-49.24, -36) * mm});
            skLineSegment(sketch, "E20.42.1", {"start": v(-49.24, -36) * mm, "end": v(-49.35, -35.85) * mm});
            skLineSegment(sketch, "E20.42.2", {"start": v(-49.46, -35.7) * mm, "end": v(-49.35, -35.85) * mm});
            skLineSegment(sketch, "E20.42.3", {"start": v(-48.12, -33.71) * mm, "end": v(-49.46, -35.7) * mm});
            skLineSegment(sketch, "E20.43.0", {"start": v(-45.02, -37.75) * mm, "end": v(-47.29, -38.53) * mm});
            skLineSegment(sketch, "E20.43.1", {"start": v(-47.29, -38.53) * mm, "end": v(-47.4, -38.39) * mm});
            skLineSegment(sketch, "E20.43.2", {"start": v(-47.52, -38.24) * mm, "end": v(-47.4, -38.39) * mm});
            skLineSegment(sketch, "E20.43.3", {"start": v(-46.29, -36.18) * mm, "end": v(-47.52, -38.24) * mm});
            skLineSegment(sketch, "E20.44.0", {"start": v(-42.98, -40.06) * mm, "end": v(-45.2, -40.96) * mm});
            skLineSegment(sketch, "E20.44.1", {"start": v(-45.2, -40.96) * mm, "end": v(-45.33, -40.82) * mm});
            skLineSegment(sketch, "E20.44.2", {"start": v(-45.46, -40.68) * mm, "end": v(-45.33, -40.82) * mm});
            skLineSegment(sketch, "E20.44.3", {"start": v(-44.33, -38.56) * mm, "end": v(-45.46, -40.68) * mm});
            skLineSegment(sketch, "E20.45.0", {"start": v(-40.82, -42.25) * mm, "end": v(-43, -43.27) * mm});
            skLineSegment(sketch, "E20.45.1", {"start": v(-43, -43.27) * mm, "end": v(-43.13, -43.13) * mm});
            skLineSegment(sketch, "E20.45.2", {"start": v(-43.27, -43) * mm, "end": v(-43.13, -43.13) * mm});
            skLineSegment(sketch, "E20.45.3", {"start": v(-42.25, -40.82) * mm, "end": v(-43.27, -43) * mm});
            skLineSegment(sketch, "E20.46.0", {"start": v(-38.56, -44.33) * mm, "end": v(-40.68, -45.46) * mm});
            skLineSegment(sketch, "E20.46.1", {"start": v(-40.68, -45.46) * mm, "end": v(-40.82, -45.33) * mm});
            skLineSegment(sketch, "E20.46.2", {"start": v(-40.96, -45.2) * mm, "end": v(-40.82, -45.33) * mm});
            skLineSegment(sketch, "E20.46.3", {"start": v(-40.06, -42.98) * mm, "end": v(-40.96, -45.2) * mm});
            skLineSegment(sketch, "E20.47.0", {"start": v(-36.18, -46.29) * mm, "end": v(-38.24, -47.52) * mm});
            skLineSegment(sketch, "E20.47.1", {"start": v(-38.24, -47.52) * mm, "end": v(-38.39, -47.4) * mm});
            skLineSegment(sketch, "E20.47.2", {"start": v(-38.53, -47.29) * mm, "end": v(-38.39, -47.4) * mm});
            skLineSegment(sketch, "E20.47.3", {"start": v(-37.75, -45.02) * mm, "end": v(-38.53, -47.29) * mm});
            skLineSegment(sketch, "E20.48.0", {"start": v(-33.71, -48.12) * mm, "end": v(-35.7, -49.46) * mm});
            skLineSegment(sketch, "E20.48.1", {"start": v(-35.7, -49.46) * mm, "end": v(-35.85, -49.35) * mm});
            skLineSegment(sketch, "E20.48.2", {"start": v(-36, -49.24) * mm, "end": v(-35.85, -49.35) * mm});
            skLineSegment(sketch, "E20.48.3", {"start": v(-35.34, -46.93) * mm, "end": v(-36, -49.24) * mm});
            skLineSegment(sketch, "E20.49.0", {"start": v(-31.15, -49.81) * mm, "end": v(-33.07, -51.26) * mm});
            skLineSegment(sketch, "E20.49.1", {"start": v(-33.07, -51.26) * mm, "end": v(-33.22, -51.16) * mm});
            skLineSegment(sketch, "E20.49.2", {"start": v(-33.38, -51.06) * mm, "end": v(-33.22, -51.16) * mm});
            skLineSegment(sketch, "E20.49.3", {"start": v(-32.84, -48.71) * mm, "end": v(-33.38, -51.06) * mm});
            skLineSegment(sketch, "E20.50.0", {"start": v(-28.5, -51.38) * mm, "end": v(-30.34, -52.92) * mm});
            skLineSegment(sketch, "E20.50.1", {"start": v(-30.34, -52.92) * mm, "end": v(-30.5, -52.83) * mm});
            skLineSegment(sketch, "E20.50.2", {"start": v(-30.66, -52.73) * mm, "end": v(-30.5, -52.83) * mm});
            skLineSegment(sketch, "E20.50.3", {"start": v(-30.24, -50.37) * mm, "end": v(-30.66, -52.73) * mm});
            skLineSegment(sketch, "E20.51.0", {"start": v(-25.77, -52.8) * mm, "end": v(-27.53, -54.44) * mm});
            skLineSegment(sketch, "E20.51.1", {"start": v(-27.53, -54.44) * mm, "end": v(-27.7, -54.35) * mm});
            skLineSegment(sketch, "E20.51.2", {"start": v(-27.86, -54.27) * mm, "end": v(-27.7, -54.35) * mm});
            skLineSegment(sketch, "E20.51.3", {"start": v(-27.57, -51.88) * mm, "end": v(-27.86, -54.27) * mm});
            skLineSegment(sketch, "E20.52.0", {"start": v(-22.97, -54.07) * mm, "end": v(-24.64, -55.8) * mm});
            skLineSegment(sketch, "E20.52.1", {"start": v(-24.64, -55.8) * mm, "end": v(-24.81, -55.73) * mm});
            skLineSegment(sketch, "E20.52.2", {"start": v(-24.98, -55.65) * mm, "end": v(-24.81, -55.73) * mm});
            skLineSegment(sketch, "E20.52.3", {"start": v(-24.81, -53.25) * mm, "end": v(-24.98, -55.65) * mm});
            skLineSegment(sketch, "E20.53.0", {"start": v(-20.1, -55.2) * mm, "end": v(-21.69, -57.02) * mm});
            skLineSegment(sketch, "E20.53.1", {"start": v(-21.69, -57.02) * mm, "end": v(-21.86, -56.95) * mm});
            skLineSegment(sketch, "E20.53.2", {"start": v(-22.04, -56.88) * mm, "end": v(-21.86, -56.95) * mm});
            skLineSegment(sketch, "E20.53.3", {"start": v(-22, -54.48) * mm, "end": v(-22.04, -56.88) * mm});
            skLineSegment(sketch, "E20.54.0", {"start": v(-17.2, -56.18) * mm, "end": v(-18.67, -58.07) * mm});
            skLineSegment(sketch, "E20.54.1", {"start": v(-18.67, -58.07) * mm, "end": v(-18.85, -58.01) * mm});
            skLineSegment(sketch, "E20.54.2", {"start": v(-19.03, -57.96) * mm, "end": v(-18.85, -58.01) * mm});
            skLineSegment(sketch, "E20.54.3", {"start": v(-19.11, -55.55) * mm, "end": v(-19.03, -57.96) * mm});
            skLineSegment(sketch, "E20.55.0", {"start": v(-14.23, -57) * mm, "end": v(-15.6, -58.97) * mm});
            skLineSegment(sketch, "E20.55.1", {"start": v(-15.6, -58.97) * mm, "end": v(-15.79, -58.92) * mm});
            skLineSegment(sketch, "E20.55.2", {"start": v(-15.97, -58.87) * mm, "end": v(-15.79, -58.92) * mm});
            skLineSegment(sketch, "E20.55.3", {"start": v(-16.18, -56.48) * mm, "end": v(-15.97, -58.87) * mm});
            skLineSegment(sketch, "E20.56.0", {"start": v(-11.23, -57.67) * mm, "end": v(-12.5, -59.7) * mm});
            skLineSegment(sketch, "E20.56.1", {"start": v(-12.5, -59.7) * mm, "end": v(-12.68, -59.67) * mm});
            skLineSegment(sketch, "E20.56.2", {"start": v(-12.87, -59.63) * mm, "end": v(-12.68, -59.67) * mm});
            skLineSegment(sketch, "E20.56.3", {"start": v(-13.2, -57.25) * mm, "end": v(-12.87, -59.63) * mm});
            skLineSegment(sketch, "E20.57.0", {"start": v(-8.2, -58.18) * mm, "end": v(-9.36, -60.28) * mm});
            skLineSegment(sketch, "E20.57.1", {"start": v(-9.36, -60.28) * mm, "end": v(-9.54, -60.25) * mm});
            skLineSegment(sketch, "E20.57.2", {"start": v(-9.73, -60.22) * mm, "end": v(-9.54, -60.25) * mm});
            skLineSegment(sketch, "E20.57.3", {"start": v(-10.19, -57.86) * mm, "end": v(-9.73, -60.22) * mm});
            skLineSegment(sketch, "E20.58.0", {"start": v(-5.14, -58.53) * mm, "end": v(-6.19, -60.69) * mm});
            skLineSegment(sketch, "E20.58.1", {"start": v(-6.19, -60.69) * mm, "end": v(-6.38, -60.67) * mm});
            skLineSegment(sketch, "E20.58.2", {"start": v(-6.56, -60.65) * mm, "end": v(-6.38, -60.67) * mm});
            skLineSegment(sketch, "E20.58.3", {"start": v(-7.14, -58.31) * mm, "end": v(-6.56, -60.65) * mm});
            skLineSegment(sketch, "E20.59.0", {"start": v(-2.07, -58.71) * mm, "end": v(-3, -60.93) * mm});
            skLineSegment(sketch, "E20.59.1", {"start": v(-3, -60.93) * mm, "end": v(-3.2, -60.92) * mm});
            skLineSegment(sketch, "E20.59.2", {"start": v(-3.38, -60.9) * mm, "end": v(-3.2, -60.92) * mm});
            skLineSegment(sketch, "E20.59.3", {"start": v(-4.08, -58.6) * mm, "end": v(-3.38, -60.9) * mm});
            skLineSegment(sketch, "E20.60.0", {"start": v(1, -58.74) * mm, "end": v(0.19, -61) * mm});
            skLineSegment(sketch, "E20.60.1", {"start": v(0.19, -61) * mm, "end": v(0, -61) * mm});
            skLineSegment(sketch, "E20.60.2", {"start": v(-0.19, -61) * mm, "end": v(0, -61) * mm});
            skLineSegment(sketch, "E20.60.3", {"start": v(-1, -58.74) * mm, "end": v(-0.19, -61) * mm});
            skLineSegment(sketch, "E20.61.0", {"start": v(4.08, -58.6) * mm, "end": v(3.38, -60.9) * mm});
            skLineSegment(sketch, "E20.61.1", {"start": v(3.38, -60.9) * mm, "end": v(3.2, -60.92) * mm});
            skLineSegment(sketch, "E20.61.2", {"start": v(3, -60.93) * mm, "end": v(3.2, -60.92) * mm});
            skLineSegment(sketch, "E20.61.3", {"start": v(2.07, -58.71) * mm, "end": v(3, -60.93) * mm});
            skLineSegment(sketch, "E20.62.0", {"start": v(7.14, -58.31) * mm, "end": v(6.56, -60.65) * mm});
            skLineSegment(sketch, "E20.62.1", {"start": v(6.56, -60.65) * mm, "end": v(6.38, -60.67) * mm});
            skLineSegment(sketch, "E20.62.2", {"start": v(6.19, -60.69) * mm, "end": v(6.38, -60.67) * mm});
            skLineSegment(sketch, "E20.62.3", {"start": v(5.14, -58.53) * mm, "end": v(6.19, -60.69) * mm});
            skLineSegment(sketch, "E20.63.0", {"start": v(10.19, -57.86) * mm, "end": v(9.73, -60.22) * mm});
            skLineSegment(sketch, "E20.63.1", {"start": v(9.73, -60.22) * mm, "end": v(9.54, -60.25) * mm});
            skLineSegment(sketch, "E20.63.2", {"start": v(9.36, -60.28) * mm, "end": v(9.54, -60.25) * mm});
            skLineSegment(sketch, "E20.63.3", {"start": v(8.2, -58.18) * mm, "end": v(9.36, -60.28) * mm});
            skLineSegment(sketch, "E20.64.0", {"start": v(13.2, -57.25) * mm, "end": v(12.87, -59.63) * mm});
            skLineSegment(sketch, "E20.64.1", {"start": v(12.87, -59.63) * mm, "end": v(12.68, -59.67) * mm});
            skLineSegment(sketch, "E20.64.2", {"start": v(12.5, -59.7) * mm, "end": v(12.68, -59.67) * mm});
            skLineSegment(sketch, "E20.64.3", {"start": v(11.23, -57.67) * mm, "end": v(12.5, -59.7) * mm});
            skLineSegment(sketch, "E20.65.0", {"start": v(16.18, -56.48) * mm, "end": v(15.97, -58.87) * mm});
            skLineSegment(sketch, "E20.65.1", {"start": v(15.97, -58.87) * mm, "end": v(15.79, -58.92) * mm});
            skLineSegment(sketch, "E20.65.2", {"start": v(15.6, -58.97) * mm, "end": v(15.79, -58.92) * mm});
            skLineSegment(sketch, "E20.65.3", {"start": v(14.23, -57) * mm, "end": v(15.6, -58.97) * mm});
            skLineSegment(sketch, "E20.66.0", {"start": v(19.11, -55.55) * mm, "end": v(19.03, -57.96) * mm});
            skLineSegment(sketch, "E20.66.1", {"start": v(19.03, -57.96) * mm, "end": v(18.85, -58.01) * mm});
            skLineSegment(sketch, "E20.66.2", {"start": v(18.67, -58.07) * mm, "end": v(18.85, -58.01) * mm});
            skLineSegment(sketch, "E20.66.3", {"start": v(17.2, -56.18) * mm, "end": v(18.67, -58.07) * mm});
            skLineSegment(sketch, "E20.67.0", {"start": v(22, -54.48) * mm, "end": v(22.04, -56.88) * mm});
            skLineSegment(sketch, "E20.67.1", {"start": v(22.04, -56.88) * mm, "end": v(21.86, -56.95) * mm});
            skLineSegment(sketch, "E20.67.2", {"start": v(21.69, -57.02) * mm, "end": v(21.86, -56.95) * mm});
            skLineSegment(sketch, "E20.67.3", {"start": v(20.1, -55.2) * mm, "end": v(21.69, -57.02) * mm});
            skLineSegment(sketch, "E20.68.0", {"start": v(24.81, -53.25) * mm, "end": v(24.98, -55.65) * mm});
            skLineSegment(sketch, "E20.68.1", {"start": v(24.98, -55.65) * mm, "end": v(24.81, -55.73) * mm});
            skLineSegment(sketch, "E20.68.2", {"start": v(24.64, -55.8) * mm, "end": v(24.81, -55.73) * mm});
            skLineSegment(sketch, "E20.68.3", {"start": v(22.97, -54.07) * mm, "end": v(24.64, -55.8) * mm});
            skLineSegment(sketch, "E20.69.0", {"start": v(27.57, -51.88) * mm, "end": v(27.86, -54.27) * mm});
            skLineSegment(sketch, "E20.69.1", {"start": v(27.86, -54.27) * mm, "end": v(27.7, -54.35) * mm});
            skLineSegment(sketch, "E20.69.2", {"start": v(27.53, -54.44) * mm, "end": v(27.7, -54.35) * mm});
            skLineSegment(sketch, "E20.69.3", {"start": v(25.77, -52.8) * mm, "end": v(27.53, -54.44) * mm});
            skLineSegment(sketch, "E20.70.0", {"start": v(30.24, -50.37) * mm, "end": v(30.66, -52.73) * mm});
            skLineSegment(sketch, "E20.70.1", {"start": v(30.66, -52.73) * mm, "end": v(30.5, -52.83) * mm});
            skLineSegment(sketch, "E20.70.2", {"start": v(30.34, -52.92) * mm, "end": v(30.5, -52.83) * mm});
            skLineSegment(sketch, "E20.70.3", {"start": v(28.5, -51.38) * mm, "end": v(30.34, -52.92) * mm});
            skLineSegment(sketch, "E20.71.0", {"start": v(32.84, -48.71) * mm, "end": v(33.38, -51.06) * mm});
            skLineSegment(sketch, "E20.71.1", {"start": v(33.38, -51.06) * mm, "end": v(33.22, -51.16) * mm});
            skLineSegment(sketch, "E20.71.2", {"start": v(33.07, -51.26) * mm, "end": v(33.22, -51.16) * mm});
            skLineSegment(sketch, "E20.71.3", {"start": v(31.15, -49.81) * mm, "end": v(33.07, -51.26) * mm});
            skLineSegment(sketch, "E20.72.0", {"start": v(35.34, -46.93) * mm, "end": v(36, -49.24) * mm});
            skLineSegment(sketch, "E20.72.1", {"start": v(36, -49.24) * mm, "end": v(35.85, -49.35) * mm});
            skLineSegment(sketch, "E20.72.2", {"start": v(35.7, -49.46) * mm, "end": v(35.85, -49.35) * mm});
            skLineSegment(sketch, "E20.72.3", {"start": v(33.71, -48.12) * mm, "end": v(35.7, -49.46) * mm});
            skLineSegment(sketch, "E20.73.0", {"start": v(37.75, -45.02) * mm, "end": v(38.53, -47.29) * mm});
            skLineSegment(sketch, "E20.73.1", {"start": v(38.53, -47.29) * mm, "end": v(38.39, -47.4) * mm});
            skLineSegment(sketch, "E20.73.2", {"start": v(38.24, -47.52) * mm, "end": v(38.39, -47.4) * mm});
            skLineSegment(sketch, "E20.73.3", {"start": v(36.18, -46.29) * mm, "end": v(38.24, -47.52) * mm});
            skLineSegment(sketch, "E20.74.0", {"start": v(40.06, -42.98) * mm, "end": v(40.96, -45.2) * mm});
            skLineSegment(sketch, "E20.74.1", {"start": v(40.96, -45.2) * mm, "end": v(40.82, -45.33) * mm});
            skLineSegment(sketch, "E20.74.2", {"start": v(40.68, -45.46) * mm, "end": v(40.82, -45.33) * mm});
            skLineSegment(sketch, "E20.74.3", {"start": v(38.56, -44.33) * mm, "end": v(40.68, -45.46) * mm});
            skLineSegment(sketch, "E20.75.0", {"start": v(42.25, -40.82) * mm, "end": v(43.27, -43) * mm});
            skLineSegment(sketch, "E20.75.1", {"start": v(43.27, -43) * mm, "end": v(43.13, -43.13) * mm});
            skLineSegment(sketch, "E20.75.2", {"start": v(43, -43.27) * mm, "end": v(43.13, -43.13) * mm});
            skLineSegment(sketch, "E20.75.3", {"start": v(40.82, -42.25) * mm, "end": v(43, -43.27) * mm});
            skLineSegment(sketch, "E20.76.0", {"start": v(44.33, -38.56) * mm, "end": v(45.46, -40.68) * mm});
            skLineSegment(sketch, "E20.76.1", {"start": v(45.46, -40.68) * mm, "end": v(45.33, -40.82) * mm});
            skLineSegment(sketch, "E20.76.2", {"start": v(45.2, -40.96) * mm, "end": v(45.33, -40.82) * mm});
            skLineSegment(sketch, "E20.76.3", {"start": v(42.98, -40.06) * mm, "end": v(45.2, -40.96) * mm});
            skLineSegment(sketch, "E20.77.0", {"start": v(46.29, -36.18) * mm, "end": v(47.52, -38.24) * mm});
            skLineSegment(sketch, "E20.77.1", {"start": v(47.52, -38.24) * mm, "end": v(47.4, -38.39) * mm});
            skLineSegment(sketch, "E20.77.2", {"start": v(47.29, -38.53) * mm, "end": v(47.4, -38.39) * mm});
            skLineSegment(sketch, "E20.77.3", {"start": v(45.02, -37.75) * mm, "end": v(47.29, -38.53) * mm});
            skLineSegment(sketch, "E20.78.0", {"start": v(48.12, -33.71) * mm, "end": v(49.46, -35.7) * mm});
            skLineSegment(sketch, "E20.78.1", {"start": v(49.46, -35.7) * mm, "end": v(49.35, -35.85) * mm});
            skLineSegment(sketch, "E20.78.2", {"start": v(49.24, -36) * mm, "end": v(49.35, -35.85) * mm});
            skLineSegment(sketch, "E20.78.3", {"start": v(46.93, -35.34) * mm, "end": v(49.24, -36) * mm});
            skLineSegment(sketch, "E20.79.0", {"start": v(49.81, -31.15) * mm, "end": v(51.26, -33.07) * mm});
            skLineSegment(sketch, "E20.79.1", {"start": v(51.26, -33.07) * mm, "end": v(51.16, -33.22) * mm});
            skLineSegment(sketch, "E20.79.2", {"start": v(51.06, -33.38) * mm, "end": v(51.16, -33.22) * mm});
            skLineSegment(sketch, "E20.79.3", {"start": v(48.71, -32.84) * mm, "end": v(51.06, -33.38) * mm});
            skLineSegment(sketch, "E20.80.0", {"start": v(51.38, -28.5) * mm, "end": v(52.92, -30.34) * mm});
            skLineSegment(sketch, "E20.80.1", {"start": v(52.92, -30.34) * mm, "end": v(52.83, -30.5) * mm});
            skLineSegment(sketch, "E20.80.2", {"start": v(52.73, -30.66) * mm, "end": v(52.83, -30.5) * mm});
            skLineSegment(sketch, "E20.80.3", {"start": v(50.37, -30.24) * mm, "end": v(52.73, -30.66) * mm});
            skLineSegment(sketch, "E20.81.0", {"start": v(52.8, -25.77) * mm, "end": v(54.44, -27.53) * mm});
            skLineSegment(sketch, "E20.81.1", {"start": v(54.44, -27.53) * mm, "end": v(54.35, -27.7) * mm});
            skLineSegment(sketch, "E20.81.2", {"start": v(54.27, -27.86) * mm, "end": v(54.35, -27.7) * mm});
            skLineSegment(sketch, "E20.81.3", {"start": v(51.88, -27.57) * mm, "end": v(54.27, -27.86) * mm});
            skLineSegment(sketch, "E20.82.0", {"start": v(54.07, -22.97) * mm, "end": v(55.8, -24.64) * mm});
            skLineSegment(sketch, "E20.82.1", {"start": v(55.8, -24.64) * mm, "end": v(55.73, -24.81) * mm});
            skLineSegment(sketch, "E20.82.2", {"start": v(55.65, -24.98) * mm, "end": v(55.73, -24.81) * mm});
            skLineSegment(sketch, "E20.82.3", {"start": v(53.25, -24.81) * mm, "end": v(55.65, -24.98) * mm});
            skLineSegment(sketch, "E20.83.0", {"start": v(55.2, -20.1) * mm, "end": v(57.02, -21.69) * mm});
            skLineSegment(sketch, "E20.83.1", {"start": v(57.02, -21.69) * mm, "end": v(56.95, -21.86) * mm});
            skLineSegment(sketch, "E20.83.2", {"start": v(56.88, -22.04) * mm, "end": v(56.95, -21.86) * mm});
            skLineSegment(sketch, "E20.83.3", {"start": v(54.48, -22) * mm, "end": v(56.88, -22.04) * mm});
            skLineSegment(sketch, "E20.84.0", {"start": v(56.18, -17.2) * mm, "end": v(58.07, -18.67) * mm});
            skLineSegment(sketch, "E20.84.1", {"start": v(58.07, -18.67) * mm, "end": v(58.01, -18.85) * mm});
            skLineSegment(sketch, "E20.84.2", {"start": v(57.96, -19.03) * mm, "end": v(58.01, -18.85) * mm});
            skLineSegment(sketch, "E20.84.3", {"start": v(55.55, -19.11) * mm, "end": v(57.96, -19.03) * mm});
            skLineSegment(sketch, "E20.85.0", {"start": v(57, -14.23) * mm, "end": v(58.97, -15.6) * mm});
            skLineSegment(sketch, "E20.85.1", {"start": v(58.97, -15.6) * mm, "end": v(58.92, -15.79) * mm});
            skLineSegment(sketch, "E20.85.2", {"start": v(58.87, -15.97) * mm, "end": v(58.92, -15.79) * mm});
            skLineSegment(sketch, "E20.85.3", {"start": v(56.48, -16.18) * mm, "end": v(58.87, -15.97) * mm});
            skLineSegment(sketch, "E20.86.0", {"start": v(57.67, -11.23) * mm, "end": v(59.7, -12.5) * mm});
            skLineSegment(sketch, "E20.86.1", {"start": v(59.7, -12.5) * mm, "end": v(59.67, -12.68) * mm});
            skLineSegment(sketch, "E20.86.2", {"start": v(59.63, -12.87) * mm, "end": v(59.67, -12.68) * mm});
            skLineSegment(sketch, "E20.86.3", {"start": v(57.25, -13.2) * mm, "end": v(59.63, -12.87) * mm});
            skLineSegment(sketch, "E20.87.0", {"start": v(58.18, -8.2) * mm, "end": v(60.28, -9.36) * mm});
            skLineSegment(sketch, "E20.87.1", {"start": v(60.28, -9.36) * mm, "end": v(60.25, -9.54) * mm});
            skLineSegment(sketch, "E20.87.2", {"start": v(60.22, -9.73) * mm, "end": v(60.25, -9.54) * mm});
            skLineSegment(sketch, "E20.87.3", {"start": v(57.86, -10.19) * mm, "end": v(60.22, -9.73) * mm});
            skLineSegment(sketch, "E20.88.0", {"start": v(58.53, -5.14) * mm, "end": v(60.69, -6.19) * mm});
            skLineSegment(sketch, "E20.88.1", {"start": v(60.69, -6.19) * mm, "end": v(60.67, -6.38) * mm});
            skLineSegment(sketch, "E20.88.2", {"start": v(60.65, -6.56) * mm, "end": v(60.67, -6.38) * mm});
            skLineSegment(sketch, "E20.88.3", {"start": v(58.31, -7.14) * mm, "end": v(60.65, -6.56) * mm});
            skLineSegment(sketch, "E20.89.0", {"start": v(58.71, -2.07) * mm, "end": v(60.93, -3) * mm});
            skLineSegment(sketch, "E20.89.1", {"start": v(60.93, -3) * mm, "end": v(60.92, -3.2) * mm});
            skLineSegment(sketch, "E20.89.2", {"start": v(60.9, -3.38) * mm, "end": v(60.92, -3.2) * mm});
            skLineSegment(sketch, "E20.89.3", {"start": v(58.6, -4.08) * mm, "end": v(60.9, -3.38) * mm});
            skLineSegment(sketch, "E20.90.0", {"start": v(58.74, 1) * mm, "end": v(61, 0.19) * mm});
            skLineSegment(sketch, "E20.90.1", {"start": v(61, 0.19) * mm, "end": v(61, 0) * mm});
            skLineSegment(sketch, "E20.90.2", {"start": v(61, -0.19) * mm, "end": v(61, 0) * mm});
            skLineSegment(sketch, "E20.90.3", {"start": v(58.74, -1) * mm, "end": v(61, -0.19) * mm});
            skLineSegment(sketch, "E20.91.0", {"start": v(58.6, 4.08) * mm, "end": v(60.9, 3.38) * mm});
            skLineSegment(sketch, "E20.91.1", {"start": v(60.9, 3.38) * mm, "end": v(60.92, 3.2) * mm});
            skLineSegment(sketch, "E20.91.2", {"start": v(60.93, 3) * mm, "end": v(60.92, 3.2) * mm});
            skLineSegment(sketch, "E20.91.3", {"start": v(58.71, 2.07) * mm, "end": v(60.93, 3) * mm});
            skLineSegment(sketch, "E20.92.0", {"start": v(58.31, 7.14) * mm, "end": v(60.65, 6.56) * mm});
            skLineSegment(sketch, "E20.92.1", {"start": v(60.65, 6.56) * mm, "end": v(60.67, 6.38) * mm});
            skLineSegment(sketch, "E20.92.2", {"start": v(60.69, 6.19) * mm, "end": v(60.67, 6.38) * mm});
            skLineSegment(sketch, "E20.92.3", {"start": v(58.53, 5.14) * mm, "end": v(60.69, 6.19) * mm});
            skLineSegment(sketch, "E20.93.0", {"start": v(57.86, 10.19) * mm, "end": v(60.22, 9.73) * mm});
            skLineSegment(sketch, "E20.93.1", {"start": v(60.22, 9.73) * mm, "end": v(60.25, 9.54) * mm});
            skLineSegment(sketch, "E20.93.2", {"start": v(60.28, 9.36) * mm, "end": v(60.25, 9.54) * mm});
            skLineSegment(sketch, "E20.93.3", {"start": v(58.18, 8.2) * mm, "end": v(60.28, 9.36) * mm});
            skLineSegment(sketch, "E20.94.0", {"start": v(57.25, 13.2) * mm, "end": v(59.63, 12.87) * mm});
            skLineSegment(sketch, "E20.94.1", {"start": v(59.63, 12.87) * mm, "end": v(59.67, 12.68) * mm});
            skLineSegment(sketch, "E20.94.2", {"start": v(59.7, 12.5) * mm, "end": v(59.67, 12.68) * mm});
            skLineSegment(sketch, "E20.94.3", {"start": v(57.67, 11.23) * mm, "end": v(59.7, 12.5) * mm});
            skLineSegment(sketch, "E20.95.0", {"start": v(56.48, 16.18) * mm, "end": v(58.87, 15.97) * mm});
            skLineSegment(sketch, "E20.95.1", {"start": v(58.87, 15.97) * mm, "end": v(58.92, 15.79) * mm});
            skLineSegment(sketch, "E20.95.2", {"start": v(58.97, 15.6) * mm, "end": v(58.92, 15.79) * mm});
            skLineSegment(sketch, "E20.95.3", {"start": v(57, 14.23) * mm, "end": v(58.97, 15.6) * mm});
            skLineSegment(sketch, "E20.96.0", {"start": v(55.55, 19.11) * mm, "end": v(57.96, 19.03) * mm});
            skLineSegment(sketch, "E20.96.1", {"start": v(57.96, 19.03) * mm, "end": v(58.01, 18.85) * mm});
            skLineSegment(sketch, "E20.96.2", {"start": v(58.07, 18.67) * mm, "end": v(58.01, 18.85) * mm});
            skLineSegment(sketch, "E20.96.3", {"start": v(56.18, 17.2) * mm, "end": v(58.07, 18.67) * mm});
            skLineSegment(sketch, "E20.97.0", {"start": v(54.48, 22) * mm, "end": v(56.88, 22.04) * mm});
            skLineSegment(sketch, "E20.97.1", {"start": v(56.88, 22.04) * mm, "end": v(56.95, 21.86) * mm});
            skLineSegment(sketch, "E20.97.2", {"start": v(57.02, 21.69) * mm, "end": v(56.95, 21.86) * mm});
            skLineSegment(sketch, "E20.97.3", {"start": v(55.2, 20.1) * mm, "end": v(57.02, 21.69) * mm});
            skLineSegment(sketch, "E20.98.0", {"start": v(53.25, 24.81) * mm, "end": v(55.65, 24.98) * mm});
            skLineSegment(sketch, "E20.98.1", {"start": v(55.65, 24.98) * mm, "end": v(55.73, 24.81) * mm});
            skLineSegment(sketch, "E20.98.2", {"start": v(55.8, 24.64) * mm, "end": v(55.73, 24.81) * mm});
            skLineSegment(sketch, "E20.98.3", {"start": v(54.07, 22.97) * mm, "end": v(55.8, 24.64) * mm});
            skLineSegment(sketch, "E20.99.0", {"start": v(51.88, 27.57) * mm, "end": v(54.27, 27.86) * mm});
            skLineSegment(sketch, "E20.99.1", {"start": v(54.27, 27.86) * mm, "end": v(54.35, 27.7) * mm});
            skLineSegment(sketch, "E20.99.2", {"start": v(54.44, 27.53) * mm, "end": v(54.35, 27.7) * mm});
            skLineSegment(sketch, "E20.99.3", {"start": v(52.8, 25.77) * mm, "end": v(54.44, 27.53) * mm});
            skLineSegment(sketch, "E20.100.0", {"start": v(50.37, 30.24) * mm, "end": v(52.73, 30.66) * mm});
            skLineSegment(sketch, "E20.100.1", {"start": v(52.73, 30.66) * mm, "end": v(52.83, 30.5) * mm});
            skLineSegment(sketch, "E20.100.2", {"start": v(52.92, 30.34) * mm, "end": v(52.83, 30.5) * mm});
            skLineSegment(sketch, "E20.100.3", {"start": v(51.38, 28.5) * mm, "end": v(52.92, 30.34) * mm});
            skLineSegment(sketch, "E20.101.0", {"start": v(48.71, 32.84) * mm, "end": v(51.06, 33.38) * mm});
            skLineSegment(sketch, "E20.101.1", {"start": v(51.06, 33.38) * mm, "end": v(51.16, 33.22) * mm});
            skLineSegment(sketch, "E20.101.2", {"start": v(51.26, 33.07) * mm, "end": v(51.16, 33.22) * mm});
            skLineSegment(sketch, "E20.101.3", {"start": v(49.81, 31.15) * mm, "end": v(51.26, 33.07) * mm});
            skLineSegment(sketch, "E20.102.0", {"start": v(46.93, 35.34) * mm, "end": v(49.24, 36) * mm});
            skLineSegment(sketch, "E20.102.1", {"start": v(49.24, 36) * mm, "end": v(49.35, 35.85) * mm});
            skLineSegment(sketch, "E20.102.2", {"start": v(49.46, 35.7) * mm, "end": v(49.35, 35.85) * mm});
            skLineSegment(sketch, "E20.102.3", {"start": v(48.12, 33.71) * mm, "end": v(49.46, 35.7) * mm});
            skLineSegment(sketch, "E20.103.0", {"start": v(45.02, 37.75) * mm, "end": v(47.29, 38.53) * mm});
            skLineSegment(sketch, "E20.103.1", {"start": v(47.29, 38.53) * mm, "end": v(47.4, 38.39) * mm});
            skLineSegment(sketch, "E20.103.2", {"start": v(47.52, 38.24) * mm, "end": v(47.4, 38.39) * mm});
            skLineSegment(sketch, "E20.103.3", {"start": v(46.29, 36.18) * mm, "end": v(47.52, 38.24) * mm});
            skLineSegment(sketch, "E20.104.0", {"start": v(42.98, 40.06) * mm, "end": v(45.2, 40.96) * mm});
            skLineSegment(sketch, "E20.104.1", {"start": v(45.2, 40.96) * mm, "end": v(45.33, 40.82) * mm});
            skLineSegment(sketch, "E20.104.2", {"start": v(45.46, 40.68) * mm, "end": v(45.33, 40.82) * mm});
            skLineSegment(sketch, "E20.104.3", {"start": v(44.33, 38.56) * mm, "end": v(45.46, 40.68) * mm});
            skLineSegment(sketch, "E20.105.0", {"start": v(40.82, 42.25) * mm, "end": v(43, 43.27) * mm});
            skLineSegment(sketch, "E20.105.1", {"start": v(43, 43.27) * mm, "end": v(43.13, 43.13) * mm});
            skLineSegment(sketch, "E20.105.2", {"start": v(43.27, 43) * mm, "end": v(43.13, 43.13) * mm});
            skLineSegment(sketch, "E20.105.3", {"start": v(42.25, 40.82) * mm, "end": v(43.27, 43) * mm});
            skLineSegment(sketch, "E20.106.0", {"start": v(38.56, 44.33) * mm, "end": v(40.68, 45.46) * mm});
            skLineSegment(sketch, "E20.106.1", {"start": v(40.68, 45.46) * mm, "end": v(40.82, 45.33) * mm});
            skLineSegment(sketch, "E20.106.2", {"start": v(40.96, 45.2) * mm, "end": v(40.82, 45.33) * mm});
            skLineSegment(sketch, "E20.106.3", {"start": v(40.06, 42.98) * mm, "end": v(40.96, 45.2) * mm});
            skLineSegment(sketch, "E20.107.0", {"start": v(36.18, 46.29) * mm, "end": v(38.24, 47.52) * mm});
            skLineSegment(sketch, "E20.107.1", {"start": v(38.24, 47.52) * mm, "end": v(38.39, 47.4) * mm});
            skLineSegment(sketch, "E20.107.2", {"start": v(38.53, 47.29) * mm, "end": v(38.39, 47.4) * mm});
            skLineSegment(sketch, "E20.107.3", {"start": v(37.75, 45.02) * mm, "end": v(38.53, 47.29) * mm});
            skLineSegment(sketch, "E20.108.0", {"start": v(33.71, 48.12) * mm, "end": v(35.7, 49.46) * mm});
            skLineSegment(sketch, "E20.108.1", {"start": v(35.7, 49.46) * mm, "end": v(35.85, 49.35) * mm});
            skLineSegment(sketch, "E20.108.2", {"start": v(36, 49.24) * mm, "end": v(35.85, 49.35) * mm});
            skLineSegment(sketch, "E20.108.3", {"start": v(35.34, 46.93) * mm, "end": v(36, 49.24) * mm});
            skLineSegment(sketch, "E20.109.0", {"start": v(31.15, 49.81) * mm, "end": v(33.07, 51.26) * mm});
            skLineSegment(sketch, "E20.109.1", {"start": v(33.07, 51.26) * mm, "end": v(33.22, 51.16) * mm});
            skLineSegment(sketch, "E20.109.2", {"start": v(33.38, 51.06) * mm, "end": v(33.22, 51.16) * mm});
            skLineSegment(sketch, "E20.109.3", {"start": v(32.84, 48.71) * mm, "end": v(33.38, 51.06) * mm});
            skLineSegment(sketch, "E20.110.0", {"start": v(28.5, 51.38) * mm, "end": v(30.34, 52.92) * mm});
            skLineSegment(sketch, "E20.110.1", {"start": v(30.34, 52.92) * mm, "end": v(30.5, 52.83) * mm});
            skLineSegment(sketch, "E20.110.2", {"start": v(30.66, 52.73) * mm, "end": v(30.5, 52.83) * mm});
            skLineSegment(sketch, "E20.110.3", {"start": v(30.24, 50.37) * mm, "end": v(30.66, 52.73) * mm});
            skLineSegment(sketch, "E20.111.0", {"start": v(25.77, 52.8) * mm, "end": v(27.53, 54.44) * mm});
            skLineSegment(sketch, "E20.111.1", {"start": v(27.53, 54.44) * mm, "end": v(27.7, 54.35) * mm});
            skLineSegment(sketch, "E20.111.2", {"start": v(27.86, 54.27) * mm, "end": v(27.7, 54.35) * mm});
            skLineSegment(sketch, "E20.111.3", {"start": v(27.57, 51.88) * mm, "end": v(27.86, 54.27) * mm});
            skLineSegment(sketch, "E20.112.0", {"start": v(22.97, 54.07) * mm, "end": v(24.64, 55.8) * mm});
            skLineSegment(sketch, "E20.112.1", {"start": v(24.64, 55.8) * mm, "end": v(24.81, 55.73) * mm});
            skLineSegment(sketch, "E20.112.2", {"start": v(24.98, 55.65) * mm, "end": v(24.81, 55.73) * mm});
            skLineSegment(sketch, "E20.112.3", {"start": v(24.81, 53.25) * mm, "end": v(24.98, 55.65) * mm});
            skLineSegment(sketch, "E20.113.0", {"start": v(20.1, 55.2) * mm, "end": v(21.69, 57.02) * mm});
            skLineSegment(sketch, "E20.113.1", {"start": v(21.69, 57.02) * mm, "end": v(21.86, 56.95) * mm});
            skLineSegment(sketch, "E20.113.2", {"start": v(22.04, 56.88) * mm, "end": v(21.86, 56.95) * mm});
            skLineSegment(sketch, "E20.113.3", {"start": v(22, 54.48) * mm, "end": v(22.04, 56.88) * mm});
            skLineSegment(sketch, "E20.114.0", {"start": v(17.2, 56.18) * mm, "end": v(18.67, 58.07) * mm});
            skLineSegment(sketch, "E20.114.1", {"start": v(18.67, 58.07) * mm, "end": v(18.85, 58.01) * mm});
            skLineSegment(sketch, "E20.114.2", {"start": v(19.03, 57.96) * mm, "end": v(18.85, 58.01) * mm});
            skLineSegment(sketch, "E20.114.3", {"start": v(19.11, 55.55) * mm, "end": v(19.03, 57.96) * mm});
            skLineSegment(sketch, "E20.115.0", {"start": v(14.23, 57) * mm, "end": v(15.6, 58.97) * mm});
            skLineSegment(sketch, "E20.115.1", {"start": v(15.6, 58.97) * mm, "end": v(15.79, 58.92) * mm});
            skLineSegment(sketch, "E20.115.2", {"start": v(15.97, 58.87) * mm, "end": v(15.79, 58.92) * mm});
            skLineSegment(sketch, "E20.115.3", {"start": v(16.18, 56.48) * mm, "end": v(15.97, 58.87) * mm});
            skLineSegment(sketch, "E20.116.0", {"start": v(11.23, 57.67) * mm, "end": v(12.5, 59.7) * mm});
            skLineSegment(sketch, "E20.116.1", {"start": v(12.5, 59.7) * mm, "end": v(12.68, 59.67) * mm});
            skLineSegment(sketch, "E20.116.2", {"start": v(12.87, 59.63) * mm, "end": v(12.68, 59.67) * mm});
            skLineSegment(sketch, "E20.116.3", {"start": v(13.2, 57.25) * mm, "end": v(12.87, 59.63) * mm});
            skLineSegment(sketch, "E20.117.0", {"start": v(8.2, 58.18) * mm, "end": v(9.36, 60.28) * mm});
            skLineSegment(sketch, "E20.117.1", {"start": v(9.36, 60.28) * mm, "end": v(9.54, 60.25) * mm});
            skLineSegment(sketch, "E20.117.2", {"start": v(9.73, 60.22) * mm, "end": v(9.54, 60.25) * mm});
            skLineSegment(sketch, "E20.117.3", {"start": v(10.19, 57.86) * mm, "end": v(9.73, 60.22) * mm});
            skLineSegment(sketch, "E20.118.0", {"start": v(5.14, 58.53) * mm, "end": v(6.19, 60.69) * mm});
            skLineSegment(sketch, "E20.118.1", {"start": v(6.19, 60.69) * mm, "end": v(6.38, 60.67) * mm});
            skLineSegment(sketch, "E20.118.2", {"start": v(6.56, 60.65) * mm, "end": v(6.38, 60.67) * mm});
            skLineSegment(sketch, "E20.118.3", {"start": v(7.14, 58.31) * mm, "end": v(6.56, 60.65) * mm});
            skLineSegment(sketch, "E20.119.0", {"start": v(2.07, 58.71) * mm, "end": v(3, 60.93) * mm});
            skLineSegment(sketch, "E20.119.1", {"start": v(3, 60.93) * mm, "end": v(3.2, 60.92) * mm});
            skLineSegment(sketch, "E20.119.2", {"start": v(3.38, 60.9) * mm, "end": v(3.2, 60.92) * mm});
            skLineSegment(sketch, "E20.119.3", {"start": v(4.08, 58.6) * mm, "end": v(3.38, 60.9) * mm});
            skCircle(sketch, "E21", {"center": v(0, 0) * mm, "radius": 7.5 * mm});
            skSolve(sketch);
        }
        {
            var Q0;
            Q0=qSketchRegion(id+"F4",true);
            extrude(context, id + "F5", {"entities" : qUnion([Q0]), "operationType" : NewBodyOperationType.ADD, "depth" : 10 * mm});
        }
        {
            var Q0;
            Q0=makeQuery(id+"F3.opExtrude","SWEPT_FACE",FACE,{"disambiguationData":[OSD([sQuery(id+"F2.wireOp",EDGE,"E12.top")])]});
            var sketch = newSketch(context, id + "F6", { "sketchPlane" : qUnion([Q0])});
            skLineSegment(sketch, "E22", {"start": v(0, 20) * mm, "end": v(0, 10) * mm, "construction": true});
            skPoint(sketch, "E22.endSnap0", {"position": v(-20, 10) * mm});
            skCircle(sketch, "E23", {"center": v(0, 10) * mm, "radius": 0.5 * mm});
            skSolve(sketch);
        }
        {
            var Q0;
            Q0=qSketchRegion(id+"F6",true);
            extrude(context, id + "F7", {"entities" : qUnion([Q0]), "operationType" : NewBodyOperationType.REMOVE, "depth" : -1 * mm});
        }
    });
